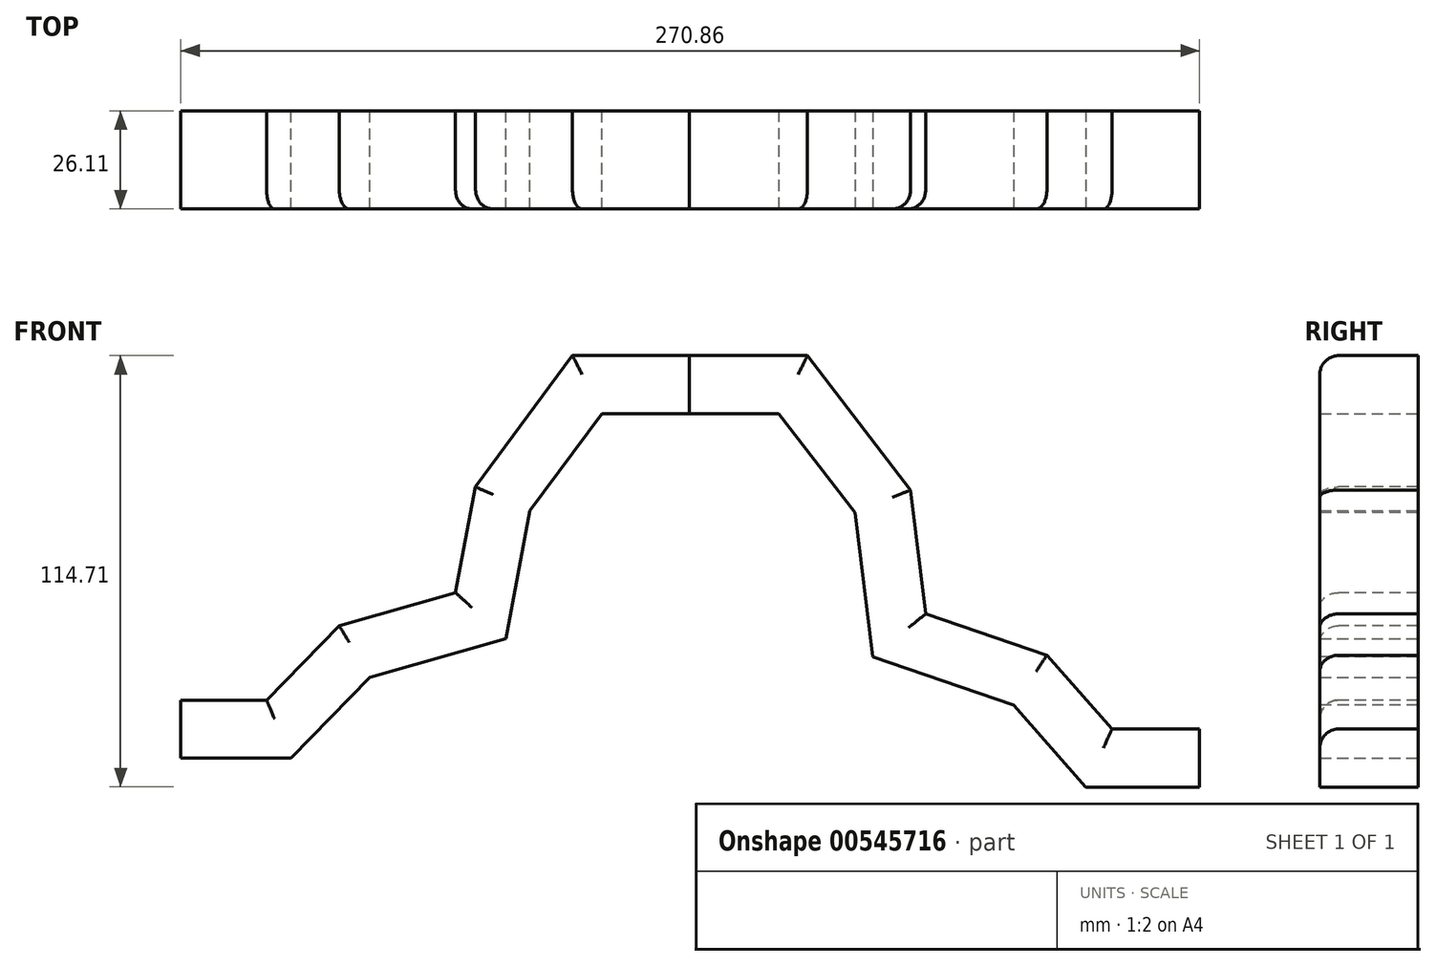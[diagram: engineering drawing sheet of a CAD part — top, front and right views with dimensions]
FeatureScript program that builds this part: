
annotation { "Feature Type Name" : "Feature", "Feature Type Description" : "" }
export const myFeature = defineFeature(function(context is Context, id is Id, definition is map)
    precondition{}
    {
        {
            var Q0;
            Q0=qCreatedBy(makeId("Right.planeOp"),FACE);
            var sketch = newSketch(context, id + "F0", { "sketchPlane" : qUnion([Q0])});
            skLineSegment(sketch, "E0.bottom", {"start": v(-6.13, 61.2) * mm, "end": v(14.98, 61.2) * mm});
            skLineSegment(sketch, "E0.top", {"start": v(-11.13, 45.8) * mm, "end": v(14.98, 45.8) * mm});
            skLineSegment(sketch, "E0.left", {"start": v(-11.13, 56.2) * mm, "end": v(-11.13, 45.8) * mm});
            skLineSegment(sketch, "E0.right", {"start": v(14.98, 61.2) * mm, "end": v(14.98, 45.8) * mm});
            skPoint(sketch, "E1.visualSharp", {"position": v(-11.13, 61.2) * mm});
            skArc(sketch, "E1.filletArc", {"start": v(-6.13, 61.2) * mm, "mid": v(-9.66, 59.74) * mm, "end": v(-11.13, 56.2) * mm});
            skSolve(sketch);
        }
        {
            var Q0;
            Q0=qCreatedBy(makeId("Front.planeOp"),FACE);
            var sketch = newSketch(context, id + "F1", { "sketchPlane" : qUnion([Q0])});
            skLineSegment(sketch, "E2", {"start": v(0, 46.23) * mm, "end": v(-23.54, 46.23) * mm});
            skLineSegment(sketch, "E3", {"start": v(-23.54, 46.23) * mm, "end": v(-42.8, 20.12) * mm});
            skLineSegment(sketch, "E4", {"start": v(-42.8, 20.12) * mm, "end": v(-49.22, -13.7) * mm});
            skLineSegment(sketch, "E5", {"start": v(-49.22, -13.7) * mm, "end": v(-85.18, -23.97) * mm});
            skLineSegment(sketch, "E6", {"start": v(-85.18, -23.97) * mm, "end": v(-106.15, -45.37) * mm});
            skLineSegment(sketch, "E7", {"start": v(-106.15, -45.37) * mm, "end": v(-135.26, -45.37) * mm});
            skSolve(sketch);
        }
        {
            var Q0;
            Q0 = qSketchRegion(id + "F0", true);
            var Q1;
            Q1 = qConstructionFilter(qBodyType(qCreatedBy(id + "F1" ,EDGE), BodyType.WIRE), ConstructionObject.NO);
            sweep(context, id + "F2", {"profiles" : qUnion([Q0]), "path" : qUnion([Q1])});
        }
        {
            var Q0;
            Q0=qCreatedBy(makeId("Front.planeOp"),FACE);
            var sketch = newSketch(context, id + "F3", { "sketchPlane" : qUnion([Q0])});
            skPoint(sketch, "E8.start.orphan", {"position": v(0, 45.37) * mm});
            skLineSegment(sketch, "E9", {"start": v(0, 45.37) * mm, "end": v(23.54, 45.37) * mm});
            skLineSegment(sketch, "E10", {"start": v(23.54, 45.37) * mm, "end": v(43.57, 19.26) * mm});
            skLineSegment(sketch, "E11", {"start": v(43.57, 19.26) * mm, "end": v(48.28, -19.26) * mm});
            skLineSegment(sketch, "E12", {"start": v(48.28, -19.26) * mm, "end": v(85.95, -32.1) * mm});
            skLineSegment(sketch, "E13", {"start": v(85.95, -32.1) * mm, "end": v(105.2, -53.93) * mm});
            skLineSegment(sketch, "E14", {"start": v(105.2, -53.93) * mm, "end": v(135.6, -53.93) * mm});
            skSolve(sketch);
        }
        {
            var Q0;
            Q0 = qSketchRegion(id + "F0", true);
            var Q1;
            Q1 = qConstructionFilter(qBodyType(qCreatedBy(id + "F3" ,EDGE), BodyType.WIRE), ConstructionObject.NO);
            sweep(context, id + "F4", {"profiles" : qUnion([Q0]), "path" : qUnion([Q1])});
        }
    });
